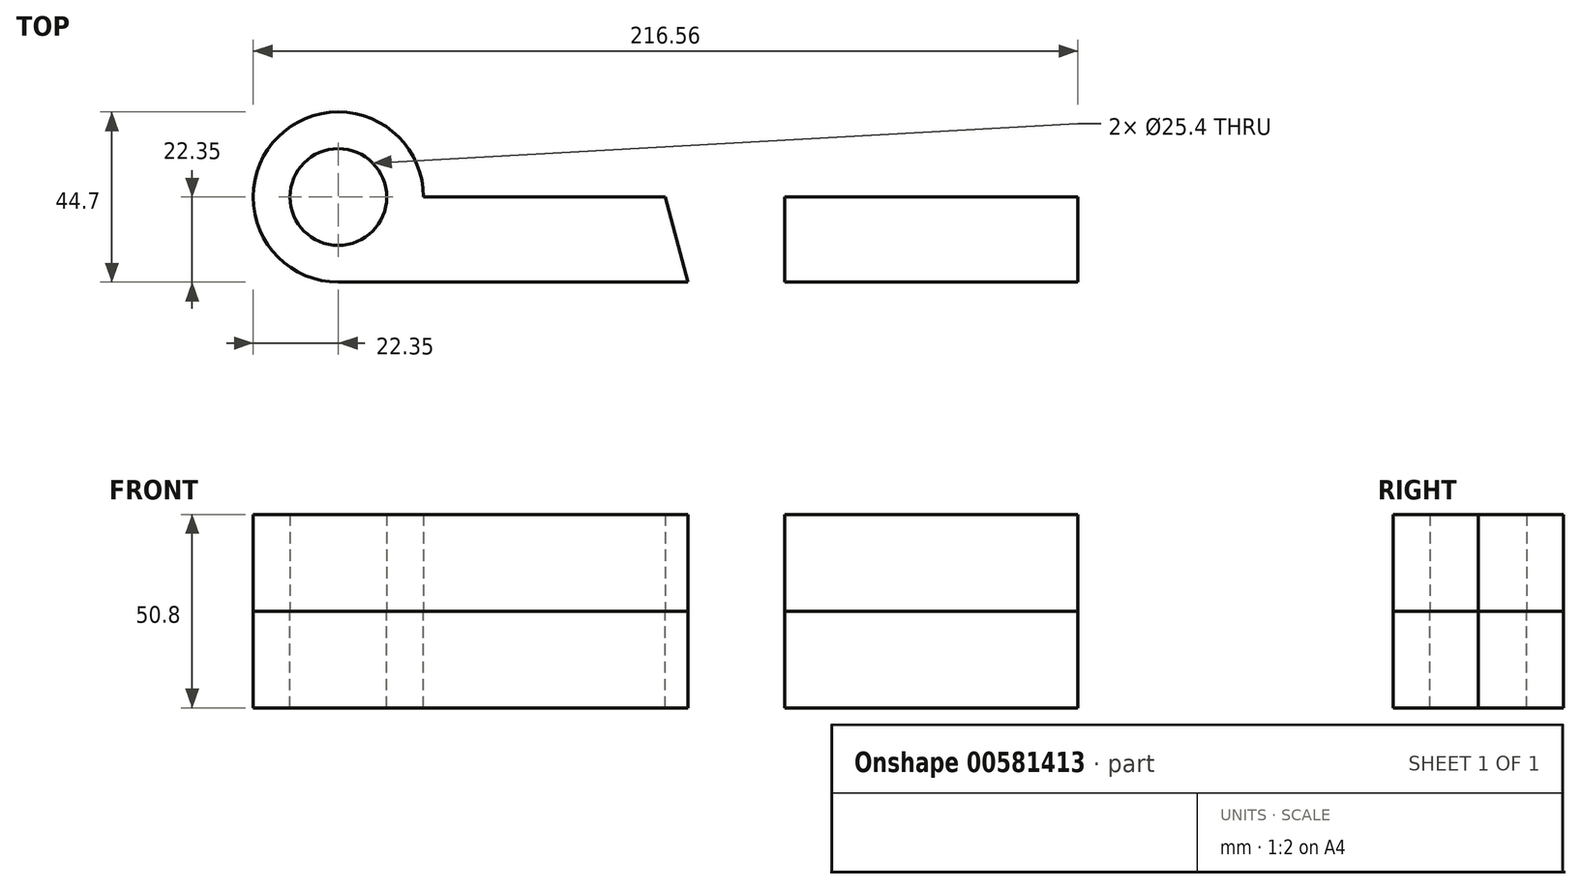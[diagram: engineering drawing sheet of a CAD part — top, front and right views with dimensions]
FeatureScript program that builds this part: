
annotation { "Feature Type Name" : "Feature", "Feature Type Description" : "" }
export const myFeature = defineFeature(function(context is Context, id is Id, definition is map)
    precondition{}
    {
        {
            var Q0;
            Q0=qCreatedBy(makeId("Top.planeOp"),FACE);
            var sketch = newSketch(context, id + "F0", { "sketchPlane" : qUnion([Q0])});
            skCircle(sketch, "E0", {"center": v(0, 0) * mm, "radius": 12.7 * mm});
            skLineSegment(sketch, "E1.bottom", {"start": v(0, 0) * mm, "end": v(194.2, 0) * mm});
            skLineSegment(sketch, "E1.top", {"start": v(0, -22.35) * mm, "end": v(194.2, -22.35) * mm});
            skLineSegment(sketch, "E1.left", {"start": v(0, 0) * mm, "end": v(0, -22.35) * mm});
            skLineSegment(sketch, "E1.right", {"start": v(194.2, 0) * mm, "end": v(194.2, -22.35) * mm});
            skCircle(sketch, "E2", {"center": v(0, 0) * mm, "radius": 22.35 * mm});
            skLineSegment(sketch, "E3", {"start": v(0, -22.35) * mm, "end": v(91.85, -22.35) * mm});
            skLineSegment(sketch, "E4", {"start": v(0, 0) * mm, "end": v(85.85, 0) * mm});
            skLineSegment(sketch, "E5", {"start": v(91.85, -22.35) * mm, "end": v(85.85, 0) * mm});
            skLineSegment(sketch, "E6", {"start": v(0, -22.35) * mm, "end": v(117.25, -22.35) * mm});
            skLineSegment(sketch, "E7", {"start": v(117.25, -22.35) * mm, "end": v(117.25, 0) * mm});
            skSolve(sketch);
        }
        {
            var Q0;
            Q0 = qSketchRegion(id + "F0", true);
            extrude(context, id + "F1", {"entities" : qUnion([Q0]), "depth" : 25.4 * mm, "offsetDistance" : 25.4 * mm});
        }
        {
            var Q0;
            {var subQ0=sQuery(id+"F0.wireOp",EDGE,"E5");Q0=makeQuery(id+"F0.imprint","IMPRINT",FACE,{"disambiguationData":[TD([[makeQuery(id+"F0.imprint","IMPRINT",EDGE,{"derivedFrom":subQ0}),-1.0]])]});}
            extrude(context, id + "F2", {"entities" : qUnion([Q0]), "operationType" : NewBodyOperationType.REMOVE, "depth" : 25.4 * mm, "offsetDistance" : 25.4 * mm});
        }
        {
            var Q0;
            Q0=makeQuery(id+"F2.boolean.opBoolean","SPLIT",BODY,{"disambiguationData":[OD(0.0)],"derivedFrom":makeQuery(id+"F1.opExtrude","SWEPT_BODY",BODY,{"disambiguationData":[OSD([sQuery(id+"F0.wireOp",EDGE,"E0"),sQuery(id+"F0.wireOp",EDGE,"E1.bottom"),sQuery(id+"F0.wireOp",EDGE,"E1.top"),sQuery(id+"F0.wireOp",EDGE,"E1.right"),sQuery(id+"F0.wireOp",EDGE,"E2"),sQuery(id+"F0.wireOp",EDGE,"E4"),sQuery(id+"F0.wireOp",EDGE,"E6")])]})});
            var Q1;
            Q1=makeQuery(id+"F2.boolean.opBoolean","SPLIT",BODY,{"disambiguationData":[OD(1.0)],"derivedFrom":makeQuery(id+"F1.opExtrude","SWEPT_BODY",BODY,{"disambiguationData":[OSD([sQuery(id+"F0.wireOp",EDGE,"E0"),sQuery(id+"F0.wireOp",EDGE,"E1.bottom"),sQuery(id+"F0.wireOp",EDGE,"E1.top"),sQuery(id+"F0.wireOp",EDGE,"E1.right"),sQuery(id+"F0.wireOp",EDGE,"E2"),sQuery(id+"F0.wireOp",EDGE,"E4"),sQuery(id+"F0.wireOp",EDGE,"E6")])]})});
            var Q2;
            Q2=qCreatedBy(makeId("Top.planeOp"),FACE);
            mirror(context, id + "F3", {"entities" : qUnion([Q0, Q1]), "mirrorPlane" : qUnion([Q2])});
        }
    });
